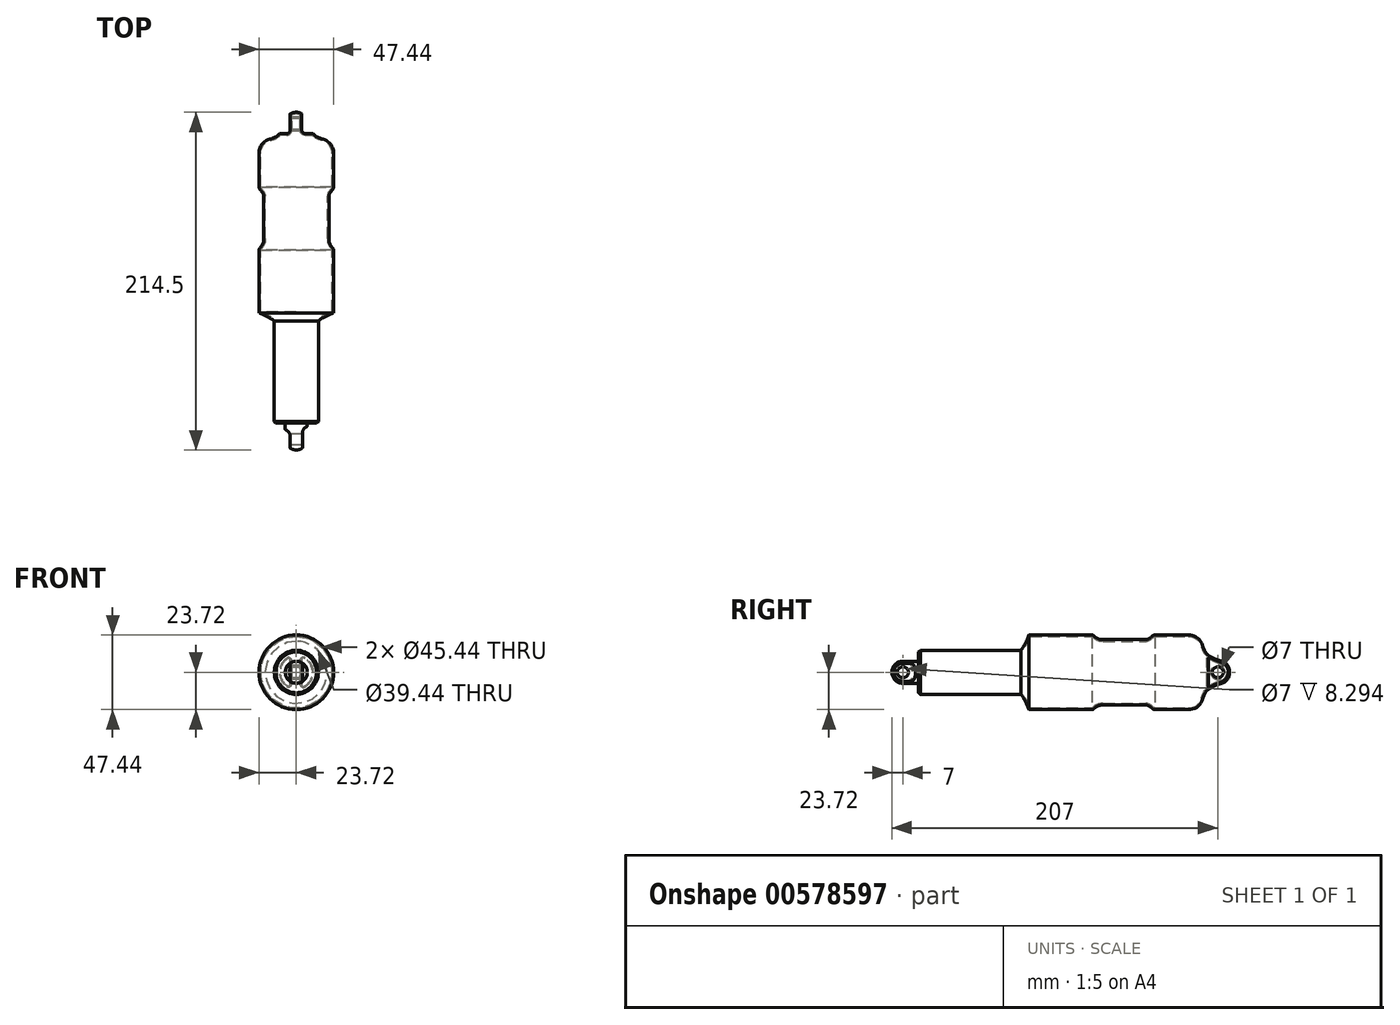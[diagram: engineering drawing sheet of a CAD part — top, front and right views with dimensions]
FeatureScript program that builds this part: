
annotation { "Feature Type Name" : "Feature", "Feature Type Description" : "" }
export const myFeature = defineFeature(function(context is Context, id is Id, definition is map)
    precondition{}
    {
        {
            var Q0;
            Q0=qCreatedBy(makeId("Right.planeOp"),FACE);
            var sketch = newSketch(context, id + "F0", { "sketchPlane" : qUnion([Q0])});
            skLineSegment(sketch, "E0", {"start": v(-120, 23.72) * mm, "end": v(-80, 23.72) * mm});
            skArc(sketch, "E1", {"start": v(7.5, 0) * mm, "mid": v(6.05, 4.43) * mm, "end": v(2.26, 7.15) * mm});
            skLineSegment(sketch, "E2", {"start": v(7.5, 0) * mm, "end": v(-125, 0) * mm});
            skLineSegment(sketch, "E3", {"start": v(-125, 0) * mm, "end": v(-125, 14) * mm});
            skArc(sketch, "E4", {"start": v(-125, 14) * mm, "mid": v(-122.12, 18.66) * mm, "end": v(-120, 23.72) * mm});
            skLineSegment(sketch, "E5", {"start": v(-72.85, 20.72) * mm, "end": v(-45.84, 20.72) * mm});
            skLineSegment(sketch, "E6.trimOffspring", {"start": v(-40, 23.72) * mm, "end": v(-18.81, 23.72) * mm});
            skLineSegment(sketch, "E7", {"start": v(43.2, 0) * mm, "end": v(-134.18, 0) * mm, "construction": true});
            skPoint(sketch, "E8.end.orphan", {"position": v(-40, 23.72) * mm});
            skFitSpline(sketch, "E9", {"points": [v(-45.84, 20.72) * mm, v(-42.63, 22.17) * mm, v(-40, 23.72) * mm], "startDerivative": vector(6.93, 0) * mm, "endDerivative": vector(6.23, 0) * mm});
            skFitSpline(sketch, "E10", {"points": [v(-80, 23.72) * mm, v(-77.4, 22) * mm, v(-72.85, 20.72) * mm], "startDerivative": vector(6.72, 0) * mm, "endDerivative": vector(9.12, 0) * mm});
            skFitSpline(sketch, "E11", {"points": [v(-18.81, 23.72) * mm, v(-11.06, 19.99) * mm, v(-7.49, 12.22) * mm, v(2.26, 7.15) * mm], "startDerivative": vector(29.69, 0) * mm, "endDerivative": vector(32.34, -10.22) * mm});
            skSolve(sketch);
        }
        {
            var Q0;
            Q0=qSketchRegion(id+"F0",true);
            var Q1;
            Q1=sQuery(id+"F0.wireOp",EDGE,"E7");
            revolve(context, id + "F1", {"entities" : qUnion([Q0]), "axis" : qUnion([Q1]), "revolveType" : RevolveType.FULL});
        }
        {
            var Q0;
            Q0=qCreatedBy(makeId("Top.planeOp"),FACE);
            var sketch = newSketch(context, id + "F2", { "sketchPlane" : qUnion([Q0])});
            skLineSegment(sketch, "E12", {"start": v(-4, 8) * mm, "end": v(-4, -4) * mm});
            skArc(sketch, "E13", {"start": v(-6, -6) * mm, "mid": v(-4.59, -5.41) * mm, "end": v(-4, -4) * mm});
            skLineSegment(sketch, "E14", {"start": v(-6, -6) * mm, "end": v(-14.05, -6) * mm});
            skLineSegment(sketch, "E15", {"start": v(-14.05, -6) * mm, "end": v(-14.05, 8) * mm});
            skLineSegment(sketch, "E16", {"start": v(-14.05, 8) * mm, "end": v(-4, 8) * mm});
            skLineSegment(sketch, "E17.bottom", {"start": v(3.5, 8) * mm, "end": v(13.54, 8) * mm});
            skLineSegment(sketch, "E17.top", {"start": v(5.5, -6) * mm, "end": v(13.54, -6) * mm});
            skLineSegment(sketch, "E17.left", {"start": v(3.5, 8) * mm, "end": v(3.5, -4) * mm});
            skLineSegment(sketch, "E17.right", {"start": v(13.54, 8) * mm, "end": v(13.54, -6) * mm});
            skArc(sketch, "E18", {"start": v(3.5, -4) * mm, "mid": v(4.08, -5.41) * mm, "end": v(5.5, -6) * mm});
            skSolve(sketch);
        }
        {
            var Q0;
            Q0=qSketchRegion(id+"F2",true);
            var Q1;
            Q1=makeQuery(id+"F1.opRevolve","SWEPT_BODY",BODY,{"disambiguationData":[OSD([sQuery(id+"F0.wireOp",EDGE,"E0"),sQuery(id+"F0.wireOp",EDGE,"E1"),sQuery(id+"F0.wireOp",EDGE,"E2"),sQuery(id+"F0.wireOp",EDGE,"E3"),sQuery(id+"F0.wireOp",EDGE,"E4"),sQuery(id+"F0.wireOp",EDGE,"E5"),sQuery(id+"F0.wireOp",EDGE,"E6.trimOffspring"),sQuery(id+"F0.wireOp",EDGE,"E9"),sQuery(id+"F0.wireOp",EDGE,"E10"),sQuery(id+"F0.wireOp",EDGE,"E11")])]});
            extrude(context, id + "F3", {"entities" : qUnion([Q0]), "operationType" : NewBodyOperationType.REMOVE, "endBound" : BoundingType.THROUGH_ALL, "oppositeDirection" : true, "depth" : 25 * mm, "endBoundEntityBody" : qUnion([Q1]), "offsetDistance" : 25 * mm, "hasSecondDirection" : true, "secondDirectionBound" : SecondDirectionBoundingType.THROUGH_ALL, "secondDirectionOppositeDirection" : false, "secondDirectionDepth" : 25 * mm});
        }
        {
            var Q0;
            Q0=makeQuery(id+"F3.boolean.opBoolean","COPY",FACE,{"derivedFrom":makeQuery(id+"F3.opExtrude","SWEPT_FACE",FACE,{"disambiguationData":[OSD([sQuery(id+"F2.wireOp",EDGE,"E12")])]})});
            var sketch = newSketch(context, id + "F4", { "sketchPlane" : qUnion([Q0])});
            skCircle(sketch, "E19", {"center": v(0, 0) * mm, "radius": 3.5 * mm});
            skSolve(sketch);
        }
        {
            var Q0;
            Q0=qSketchRegion(id+"F4",true);
            extrude(context, id + "F5", {"entities" : qUnion([Q0]), "operationType" : NewBodyOperationType.REMOVE, "endBound" : BoundingType.THROUGH_ALL, "oppositeDirection" : true, "depth" : 25 * mm, "offsetDistance" : 25 * mm, "hasSecondDirection" : true, "secondDirectionBound" : SecondDirectionBoundingType.THROUGH_ALL, "secondDirectionOppositeDirection" : false, "secondDirectionDepth" : 25 * mm});
        }
        {
            var Q0;
            Q0=makeQuery(id+"F1.opRevolve","SWEPT_FACE",FACE,{"disambiguationData":[OSD([sQuery(id+"F0.wireOp",EDGE,"E3")])]});
            var Q1;
            Q1=makeQuery(id+"F1.opRevolve","SWEPT_BODY",BODY,{"disambiguationData":[OSD([sQuery(id+"F0.wireOp",EDGE,"E0"),sQuery(id+"F0.wireOp",EDGE,"E1"),sQuery(id+"F0.wireOp",EDGE,"E2"),sQuery(id+"F0.wireOp",EDGE,"E3"),sQuery(id+"F0.wireOp",EDGE,"E4"),sQuery(id+"F0.wireOp",EDGE,"E5"),sQuery(id+"F0.wireOp",EDGE,"E6.trimOffspring"),sQuery(id+"F0.wireOp",EDGE,"E9"),sQuery(id+"F0.wireOp",EDGE,"E10"),sQuery(id+"F0.wireOp",EDGE,"E11")])]});
            shell(context, id + "F6", {"entities" : qUnion([Q0]), "parts" : qUnion([Q1]), "thickness" : 1 * mm});
        }
        {
            var Q0;
            Q0=qCreatedBy(makeId("Right.planeOp"),FACE);
            var sketch = newSketch(context, id + "F7", { "sketchPlane" : qUnion([Q0])});
            skLineSegment(sketch, "E20", {"start": v(32.28, 0) * mm, "end": v(-200, 0) * mm, "construction": true});
            skLineSegment(sketch, "E21.bottom", {"start": v(-200, 0) * mm, "end": v(-125, 0) * mm});
            skLineSegment(sketch, "E21.top", {"start": v(-190, 14) * mm, "end": v(-125, 14) * mm});
            skLineSegment(sketch, "E21.right", {"start": v(-125, 0) * mm, "end": v(-125, 14) * mm});
            skLineSegment(sketch, "E22", {"start": v(0, 18.93) * mm, "end": v(0, -37.33) * mm, "construction": true});
            skLineSegment(sketch, "E23", {"start": v(-190, 14) * mm, "end": v(-190, 7) * mm});
            skLineSegment(sketch, "E24", {"start": v(-190, 7) * mm, "end": v(-200, 7) * mm});
            skLineSegment(sketch, "E25", {"start": v(-200, 0) * mm, "end": v(-207, 0) * mm});
            skArc(sketch, "E26", {"start": v(-200, 7) * mm, "mid": v(-204.95, 4.95) * mm, "end": v(-207, 0) * mm});
            skSolve(sketch);
        }
        {
            var Q0;
            Q0=qSketchRegion(id+"F7",true);
            var Q1;
            Q1=sQuery(id+"F7.wireOp",EDGE,"E20");
            revolve(context, id + "F8", {"entities" : qUnion([Q0]), "axis" : qUnion([Q1]), "revolveType" : RevolveType.FULL});
        }
        {
            var Q0;
            Q0=qCreatedBy(makeId("Top.planeOp"),FACE);
            var sketch = newSketch(context, id + "F9", { "sketchPlane" : qUnion([Q0])});
            skLineSegment(sketch, "E27", {"start": v(-51.4, 0) * mm, "end": v(123.75, 0) * mm, "construction": true});
            skLineSegment(sketch, "E28", {"start": v(0, 55.27) * mm, "end": v(0, -227.86) * mm, "construction": true});
            skLineSegment(sketch, "E29.bottom", {"start": v(4, -210) * mm, "end": v(20, -210) * mm});
            skLineSegment(sketch, "E29.top", {"start": v(8, -192) * mm, "end": v(20, -192) * mm});
            skLineSegment(sketch, "E29.left", {"start": v(4, -210) * mm, "end": v(4, -196) * mm});
            skLineSegment(sketch, "E29.right", {"start": v(20, -210) * mm, "end": v(20, -192) * mm});
            skArc(sketch, "E30", {"start": v(8, -192) * mm, "mid": v(5.17, -193.17) * mm, "end": v(4, -196) * mm});
            skLineSegment(sketch, "E31.bottom", {"start": v(-20, -194) * mm, "end": v(-8, -194) * mm});
            skLineSegment(sketch, "E31.top", {"start": v(-20, -212) * mm, "end": v(-4, -212) * mm});
            skLineSegment(sketch, "E31.left", {"start": v(-20, -194) * mm, "end": v(-20, -212) * mm});
            skLineSegment(sketch, "E31.right", {"start": v(-4, -198) * mm, "end": v(-4, -212) * mm});
            skArc(sketch, "E32", {"start": v(-4, -198) * mm, "mid": v(-5.17, -195.17) * mm, "end": v(-8, -194) * mm});
            skSolve(sketch);
        }
        {
            var Q0;
            Q0=qSketchRegion(id+"F9",true);
            extrude(context, id + "F10", {"entities" : qUnion([Q0]), "operationType" : NewBodyOperationType.REMOVE, "endBound" : BoundingType.THROUGH_ALL, "oppositeDirection" : true, "depth" : 25 * mm, "offsetDistance" : 25 * mm, "hasSecondDirection" : true, "secondDirectionBound" : SecondDirectionBoundingType.THROUGH_ALL, "secondDirectionOppositeDirection" : false, "secondDirectionDepth" : 25 * mm});
        }
        {
            var Q0;
            Q0=makeQuery(id+"F8.opRevolve","SWEPT_EDGE",EDGE,{"disambiguationData":[OSD([sQuery(id+"F7.wireOp",EDGE,"E21.top"),sQuery(id+"F7.wireOp",EDGE,"E23")])]});
            chamfer(context, id + "F11", {"entities" : qUnion([Q0]), "width" : 1 * mm, "tangentPropagation" : true});
        }
        {
            var Q0;
            Q0=makeQuery(id+"F8.opRevolve","SWEPT_EDGE",EDGE,{"disambiguationData":[OSD([sQuery(id+"F7.wireOp",EDGE,"E23"),sQuery(id+"F7.wireOp",EDGE,"E24")])]});
            fillet(context, id + "F12", {"entities" : qUnion([Q0]), "radius" : 1 * mm, "tangentPropagation" : true, "allowEdgeOverflow" : false});
        }
        {
            var Q0;
            Q0=qCreatedBy(makeId("Right.planeOp"),FACE);
            var sketch = newSketch(context, id + "F13", { "sketchPlane" : qUnion([Q0])});
            skCircle(sketch, "E33", {"center": v(-200, 0) * mm, "radius": 3.5 * mm});
            skSolve(sketch);
        }
        {
            var Q0;
            Q0=qSketchRegion(id+"F13",true);
            extrude(context, id + "F14", {"entities" : qUnion([Q0]), "operationType" : NewBodyOperationType.REMOVE, "endBound" : BoundingType.THROUGH_ALL, "oppositeDirection" : true, "depth" : 25 * mm, "offsetDistance" : 25 * mm, "hasSecondDirection" : true, "secondDirectionBound" : SecondDirectionBoundingType.THROUGH_ALL, "secondDirectionOppositeDirection" : false, "secondDirectionDepth" : 25 * mm});
        }
    });
